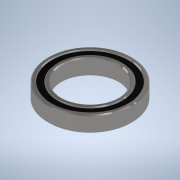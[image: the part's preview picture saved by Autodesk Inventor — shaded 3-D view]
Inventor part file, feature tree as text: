
AUTODESK INVENTOR PART (.ipt)
format: ipt  version: 2022 (Build 260153000, 153)  size: 186,880 bytes
history: native  units: mm
features: extrude x3, sketch x3, chamfer x2, other x1, projected_geometry x1
ambient origin geometry x8: Origin, YZ Plane, XZ Plane, XY Plane, X Axis, Y Axis, Z Axis, Center Point
bodies: Body1 (feature_tree)
feature tree (10):
  other  "Твердое тело1"
  extrude  "Выдавливание1"  Depth=25.0mm
  extrude  "Выдавливание2"  Depth=37.0mm
  chamfer  "Фаска2"  Distance=7.0mm
  extrude  "Выдавливание3"  Depth=2.6mm
  chamfer  "Фаска1"  Distance=1.7mm
  sketch  "Эскиз1"
  sketch  "Эскиз2"
  sketch  "Эскиз3"
  projected_geometry  "Спроецированная петля1"
